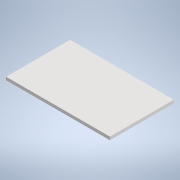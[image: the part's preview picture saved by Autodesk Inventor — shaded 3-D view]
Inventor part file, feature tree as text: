
AUTODESK INVENTOR PART (.ipt)
format: ipt  version: 2021 (Build 250183000, 183)  size: 96,256 bytes
history: native  units: in
note: dims shown in document units (in); Inventor stores cm internally (conversion verified against a paired STEP export)
features: extrude x2, sketch x2
ambient origin geometry x8: Origin, YZ Plane, XZ Plane, XY Plane, X Axis, Y Axis, Z Axis, Center Point
bodies: Solid1 (feature_tree)
feature tree (4):
  extrude  "Extrusion1"  Depth=1.0in TaperAngle=0.0deg
  extrude  "Extrusion2"  [1 undecoded]
  sketch  "Sketch1"  dims[d2=16.9291in d3=0.0in d4=1.0in d5=0.0in]
  sketch  "Sketch2"
note: 1 required parameter value undecoded (feature->parameter linkage not recoverable at this tier; creation-order binding heuristic only, values carry confidence <= 0.55)
